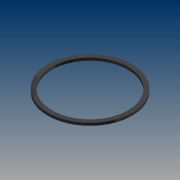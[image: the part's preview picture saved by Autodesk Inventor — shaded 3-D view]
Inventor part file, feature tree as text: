
AUTODESK INVENTOR PART (.ipt)
format: ipt  version: 2014 (Build 180170000, 170)  size: 77,312 bytes
history: native  units: mm
features: extrude x1, sketch x1
ambient origin geometry x8: Origin, YZ Plane, XZ Plane, XY Plane, X Axis, Y Axis, Z Axis, Center Point
bodies: Solid1 (feature_tree)
feature tree (2):
  extrude  "Extrusion1"  Depth=2.5mm
  sketch  "Sketch1"  dims[d0=80.0mm d1=72.0mm d2=2.5mm d3=0.0mm]
